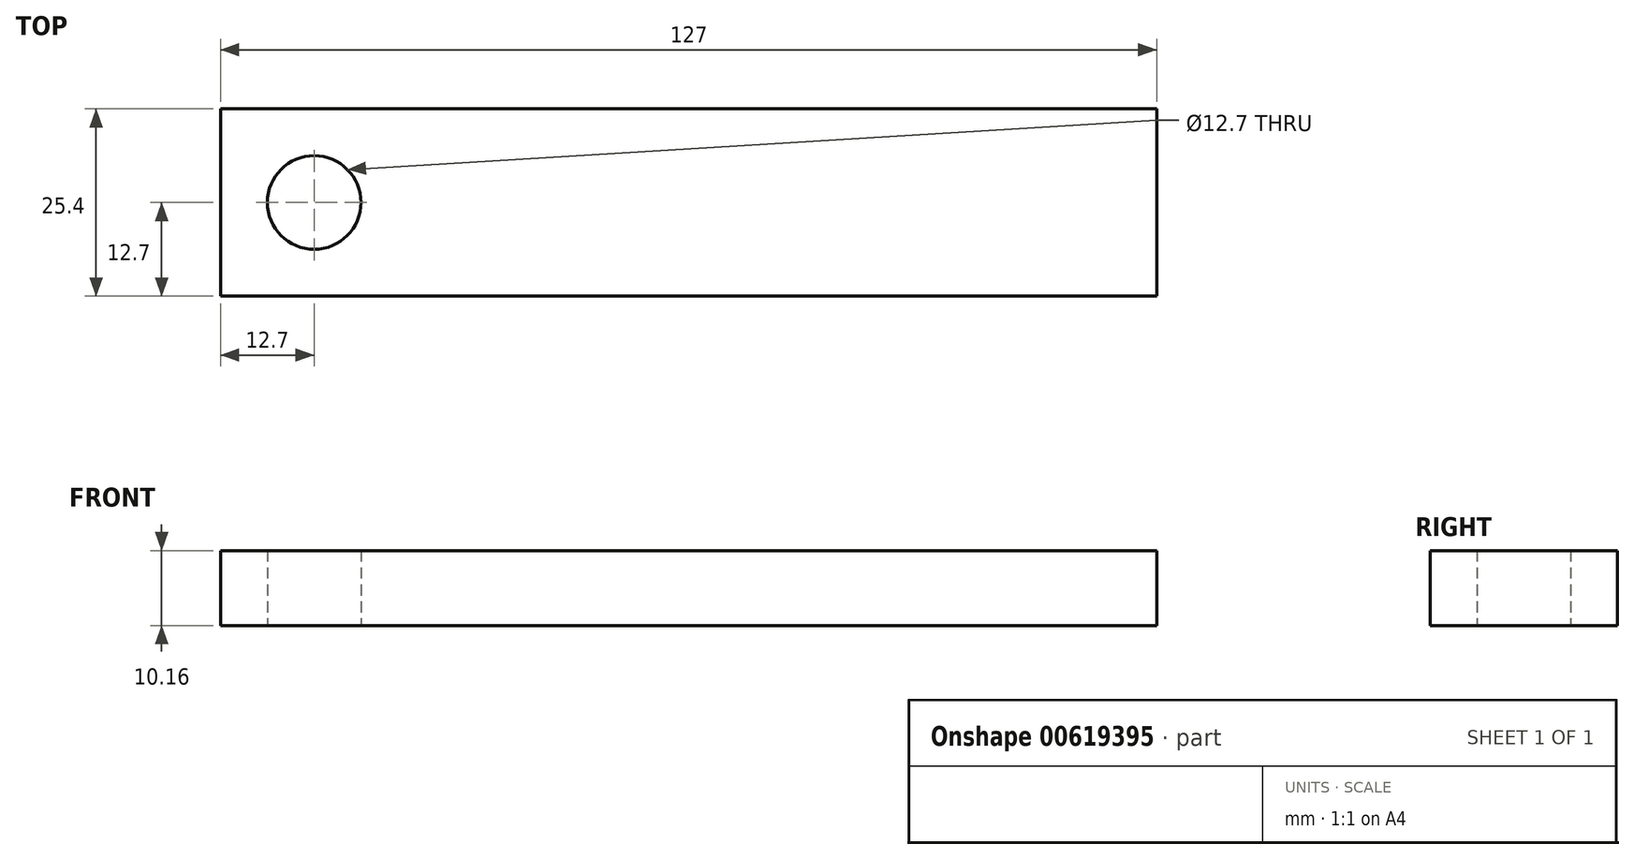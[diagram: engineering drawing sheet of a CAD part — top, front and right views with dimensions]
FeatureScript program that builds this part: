
annotation { "Feature Type Name" : "Feature", "Feature Type Description" : "" }
export const myFeature = defineFeature(function(context is Context, id is Id, definition is map)
    precondition{}
    {
        {
            var Q0;
            Q0=qCreatedBy(makeId("Top.planeOp"),FACE);
            var sketch = newSketch(context, id + "F0", { "sketchPlane" : qUnion([Q0])});
            skLineSegment(sketch, "E0.bottom", {"start": v(0, -12.7) * mm, "end": v(127, -12.7) * mm});
            skLineSegment(sketch, "E0.top", {"start": v(0, 12.7) * mm, "end": v(127, 12.7) * mm});
            skLineSegment(sketch, "E0.left", {"start": v(0, -12.7) * mm, "end": v(0, 12.7) * mm});
            skLineSegment(sketch, "E0.right", {"start": v(127, -12.7) * mm, "end": v(127, 12.7) * mm});
            skCircle(sketch, "E1", {"center": v(12.7, 0) * mm, "radius": 6.35 * mm});
            skSolve(sketch);
        }
        {
            var Q0;
            Q0=makeQuery(id+"F0.imprint","IMPRINT",FACE,{"disambiguationData":[TD([[makeQuery(id+"F0.imprint","IMPRINT",EDGE,{"derivedFrom":sQuery(id+"F0.wireOp",EDGE,"E0.bottom")}),1.0]])]});
            extrude(context, id + "F1", {"entities" : qUnion([Q0]), "depth" : 10.16 * mm, "offsetDistance" : 25.4 * mm});
        }
    });
